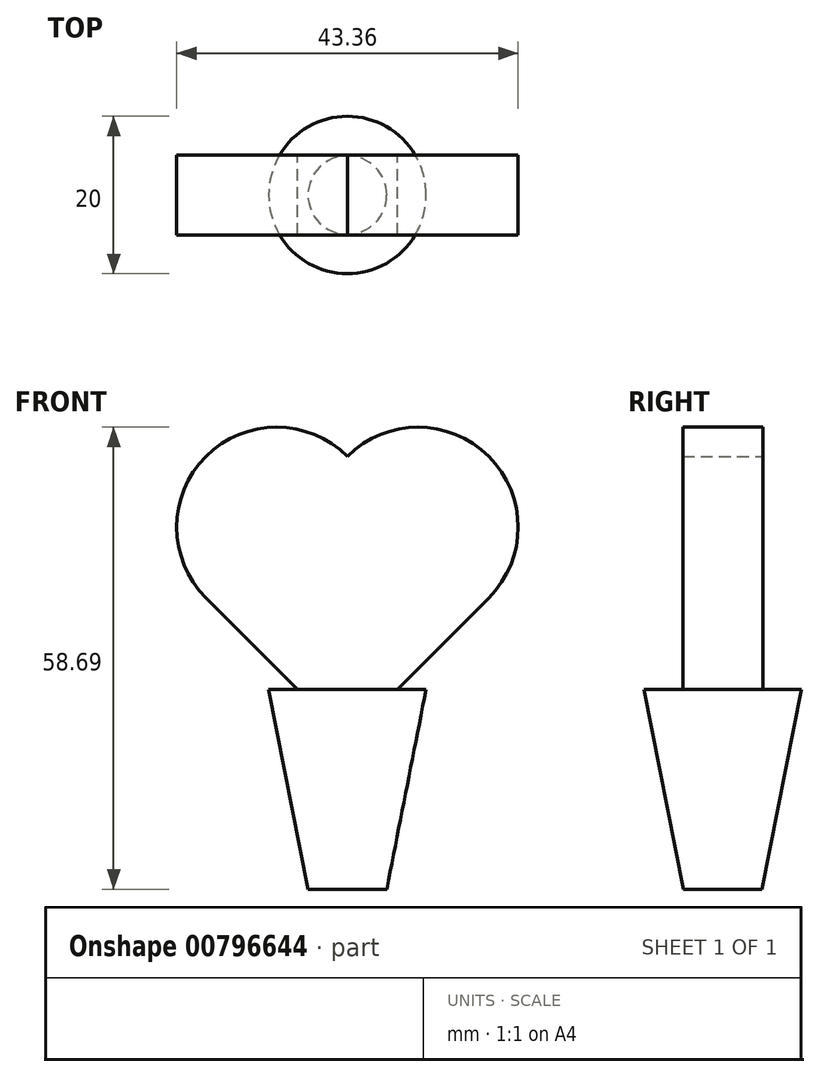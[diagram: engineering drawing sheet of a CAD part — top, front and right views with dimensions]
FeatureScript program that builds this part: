
annotation { "Feature Type Name" : "Feature", "Feature Type Description" : "" }
export const myFeature = defineFeature(function(context is Context, id is Id, definition is map)
    precondition{}
    {
        {
            var Q0;
            Q0=qCreatedBy(makeId("Top.planeOp"),FACE);
            var sketch = newSketch(context, id + "F0", { "sketchPlane" : qUnion([Q0])});
            skCircle(sketch, "E0", {"center": v(0, 0) * mm, "radius": 5 * mm});
            skSolve(sketch);
        }
        {
            var Q0;
            Q0=qCreatedBy(makeId("Top.planeOp"),FACE);
            cPlane(context, id + "F1", {"entities" : qUnion([Q0]), "cplaneType" : CPlaneType.OFFSET, "offset" : 25.4 * mm, "width" : 152.4 * mm, "height" : 152.4 * mm});
        }
        {
            var Q0;
            Q0=qCreatedBy(id+"F1.planeOp",FACE);
            var sketch = newSketch(context, id + "F2", { "sketchPlane" : qUnion([Q0])});
            skCircle(sketch, "E1", {"center": v(0, 0) * mm, "radius": 10 * mm});
            skSolve(sketch);
        }
        {
            var Q0;
            Q0=makeQuery(id+"F0.imprint","IMPRINT",FACE,{"disambiguationData":[TD([[makeQuery(id+"F0.imprint","IMPRINT",EDGE,{"derivedFrom":sQuery(id+"F0.wireOp",EDGE,"E0")}),1.0]])]});
            var Q1;
            Q1=makeQuery(id+"F2.imprint","IMPRINT",FACE,{"disambiguationData":[TD([[makeQuery(id+"F2.imprint","IMPRINT",EDGE,{"derivedFrom":sQuery(id+"F2.wireOp",EDGE,"E1")}),1.0]])]});
            loft(context, id + "F3", {"sheetProfilesArray" : [{ "sheetProfileEntities" : qUnion([Q0]) }, { "sheetProfileEntities" : qUnion([Q1]) }]});
        }
        {
            var Q0;
            Q0=qCreatedBy(makeId("Front.planeOp"),FACE);
            var sketch = newSketch(context, id + "F4", { "sketchPlane" : qUnion([Q0])});
            skLineSegment(sketch, "E2", {"start": v(0, 19.05) * mm, "end": v(-17.96, 37.01) * mm, "construction": true});
            skLineSegment(sketch, "E3", {"start": v(-17.96, 37.01) * mm, "end": v(17.96, 37.01) * mm, "construction": true});
            skLineSegment(sketch, "E4", {"start": v(17.96, 37.01) * mm, "end": v(0, 19.05) * mm, "construction": true});
            skPoint(sketch, "E5", {"position": v(0, 37.01) * mm});
            skPoint(sketch, "E6", {"position": v(0, 19.05) * mm});
            skLineSegment(sketch, "E7", {"start": v(-17.96, 37.01) * mm, "end": v(0, 54.97) * mm, "construction": true});
            skLineSegment(sketch, "E8", {"start": v(0, 54.97) * mm, "end": v(17.96, 37.01) * mm, "construction": true});
            skArc(sketch, "E9", {"start": v(0, 54.97) * mm, "mid": v(-17.96, 54.97) * mm, "end": v(-17.96, 37.01) * mm});
            skArc(sketch, "E10", {"start": v(17.96, 37.01) * mm, "mid": v(17.96, 54.97) * mm, "end": v(0, 54.97) * mm});
            skLineSegment(sketch, "E11", {"start": v(-17.96, 37.01) * mm, "end": v(0, 19.05) * mm});
            skLineSegment(sketch, "E12", {"start": v(17.96, 37.01) * mm, "end": v(0, 19.05) * mm});
            skSolve(sketch);
        }
        {
            var Q0;
            Q0=makeQuery(id+"F4.imprint","IMPRINT",FACE,{"disambiguationData":[TD([[makeQuery(id+"F4.imprint","IMPRINT",EDGE,{"derivedFrom":sQuery(id+"F4.wireOp",EDGE,"E9")}),1.0]])]});
            extrude(context, id + "F5", {"entities" : qUnion([Q0]), "operationType" : NewBodyOperationType.ADD, "depth" : 5.08 * mm, "offsetDistance" : 25.4 * mm});
        }
        {
            var Q0;
            Q0 = qSketchRegion(id + "F4", true);
            extrude(context, id + "F6", {"entities" : qUnion([Q0]), "operationType" : NewBodyOperationType.ADD, "oppositeDirection" : true, "depth" : 5.08 * mm, "offsetDistance" : 25.4 * mm});
        }
    });
